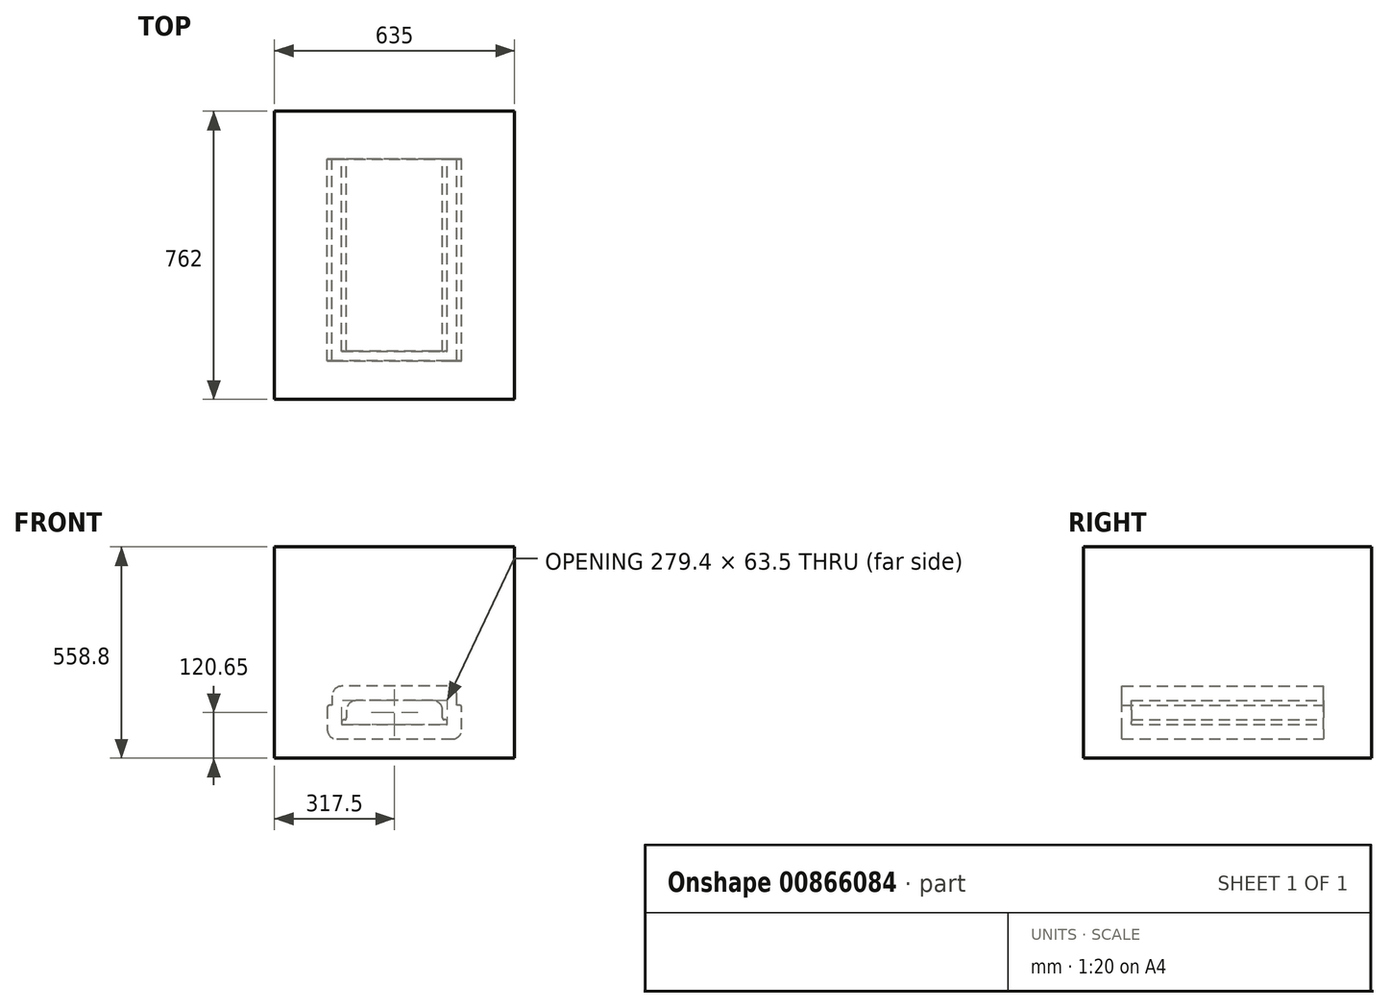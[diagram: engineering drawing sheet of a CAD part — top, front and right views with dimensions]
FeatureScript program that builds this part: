
annotation { "Feature Type Name" : "Feature", "Feature Type Description" : "" }
export const myFeature = defineFeature(function(context is Context, id is Id, definition is map)
    precondition{}
    {
        {
            var Q0;
            Q0=qCreatedBy(makeId("Front.planeOp"),FACE);
            var sketch = newSketch(context, id + "F0", { "sketchPlane" : qUnion([Q0])});
            skLineSegment(sketch, "E0", {"start": v(139.7, 0) * mm, "end": v(139.7, 12.7) * mm});
            skLineSegment(sketch, "E1", {"start": v(139.7, 12.7) * mm, "end": v(127, 12.7) * mm});
            skLineSegment(sketch, "E2", {"start": v(127, 12.7) * mm, "end": v(127, 63.5) * mm});
            skLineSegment(sketch, "E3", {"start": v(127, 63.5) * mm, "end": v(-127, 63.5) * mm});
            skLineSegment(sketch, "E4", {"start": v(-127, 63.5) * mm, "end": v(-127, 12.7) * mm});
            skLineSegment(sketch, "E5", {"start": v(-127, 12.7) * mm, "end": v(-139.7, 12.7) * mm});
            skLineSegment(sketch, "E6", {"start": v(-139.7, 12.7) * mm, "end": v(-139.7, 0) * mm});
            skLineSegment(sketch, "E7", {"start": v(0, 0) * mm, "end": v(0, 63.5) * mm, "construction": true});
            skLineSegment(sketch, "E8.0", {"start": v(-177.8, 50.8) * mm, "end": v(-177.8, 0) * mm});
            skLineSegment(sketch, "E8.1", {"start": v(-165.1, 50.8) * mm, "end": v(-177.8, 50.8) * mm});
            skLineSegment(sketch, "E8.2", {"start": v(-165.1, 101.6) * mm, "end": v(-165.1, 50.8) * mm});
            skLineSegment(sketch, "E8.3", {"start": v(177.8, 0) * mm, "end": v(177.8, 50.8) * mm});
            skLineSegment(sketch, "E8.4", {"start": v(177.8, 50.8) * mm, "end": v(165.1, 50.8) * mm});
            skLineSegment(sketch, "E8.5", {"start": v(165.1, 50.8) * mm, "end": v(165.1, 101.6) * mm});
            skLineSegment(sketch, "E8.6", {"start": v(165.1, 101.6) * mm, "end": v(-165.1, 101.6) * mm});
            skLineSegment(sketch, "E9", {"start": v(-177.8, 0) * mm, "end": v(-139.7, 0) * mm});
            skLineSegment(sketch, "E10", {"start": v(139.7, 0) * mm, "end": v(177.8, 0) * mm});
            skSolve(sketch);
        }
        {
            var Q0;
            Q0 = qSketchRegion(id + "F0", true);
            var Q1;
            Q1 = qConstructionFilter(qBodyType(qCreatedBy(id + "F0" ,EDGE), BodyType.WIRE), ConstructionObject.NO);
            extrude(context, id + "F1", {"entities" : qUnion([Q0]), "surfaceEntities" : qUnion([Q1]), "endBound" : BoundingType.SYMMETRIC, "depth" : 508 * mm, "offsetDistance" : 25.4 * mm});
        }
        {
            var Q0;
            Q0=makeQuery(id+"F1.opExtrude","SWEPT_FACE",FACE,{"disambiguationData":[OSD([sQuery(id+"F0.wireOp",EDGE,"E9")])]});
            var sketch = newSketch(context, id + "F2", { "sketchPlane" : qUnion([Q0])});
            skLineSegment(sketch, "E11.bottom", {"start": v(-177.8, 254) * mm, "end": v(177.8, 254) * mm});
            skLineSegment(sketch, "E11.top", {"start": v(-177.8, -254) * mm, "end": v(177.8, -254) * mm});
            skLineSegment(sketch, "E11.left", {"start": v(-177.8, 254) * mm, "end": v(-177.8, -254) * mm});
            skLineSegment(sketch, "E11.right", {"start": v(177.8, 254) * mm, "end": v(177.8, -254) * mm});
            skSolve(sketch);
        }
        {
            var Q0;
            Q0 = qSketchRegion(id + "F2", true);
            extrude(context, id + "F3", {"entities" : qUnion([Q0]), "operationType" : NewBodyOperationType.ADD, "depth" : 38.1 * mm, "offsetDistance" : 25.4 * mm});
        }
        {
            var Q0;
            Q0=makeQuery(id+"F1.opExtrude","SWEPT_EDGE",EDGE,{"disambiguationData":[OSD([sQuery(id+"F0.wireOp",EDGE,"E4"),sQuery(id+"F0.wireOp",EDGE,"E5")])]});
            var Q1;
            Q1=makeQuery(id+"F1.opExtrude","SWEPT_EDGE",EDGE,{"disambiguationData":[OSD([sQuery(id+"F0.wireOp",EDGE,"E1"),sQuery(id+"F0.wireOp",EDGE,"E2")])]});
            var Q2;
            Q2=makeQuery(id+"F1.opExtrude","SWEPT_EDGE",EDGE,{"disambiguationData":[OSD([sQuery(id+"F0.wireOp",EDGE,"E0"),sQuery(id+"F0.wireOp",EDGE,"E1")])]});
            var Q3;
            Q3=makeQuery(id+"F1.opExtrude","SWEPT_EDGE",EDGE,{"disambiguationData":[OSD([sQuery(id+"F0.wireOp",EDGE,"E0"),sQuery(id+"F0.wireOp",EDGE,"E10")])]});
            var Q4;
            Q4=makeQuery(id+"F1.opExtrude","SWEPT_EDGE",EDGE,{"disambiguationData":[OSD([sQuery(id+"F0.wireOp",EDGE,"E5"),sQuery(id+"F0.wireOp",EDGE,"E6")])]});
            var Q5;
            Q5=makeQuery(id+"F1.opExtrude","SWEPT_EDGE",EDGE,{"disambiguationData":[OSD([sQuery(id+"F0.wireOp",EDGE,"E6"),sQuery(id+"F0.wireOp",EDGE,"E9")])]});
            var Q6;
            Q6=makeQuery(id+"F1.opExtrude","SWEPT_EDGE",EDGE,{"disambiguationData":[OSD([sQuery(id+"F0.wireOp",EDGE,"E8.0"),sQuery(id+"F0.wireOp",EDGE,"E8.1")])]});
            var Q7;
            Q7=makeQuery(id+"F1.opExtrude","SWEPT_EDGE",EDGE,{"disambiguationData":[OSD([sQuery(id+"F0.wireOp",EDGE,"E8.3"),sQuery(id+"F0.wireOp",EDGE,"E8.4")])]});
            fillet(context, id + "F4", {"entities" : qUnion([Q0, Q1, Q2, Q3, Q4, Q5, Q6, Q7]), "radius" : 5.08 * mm, "tangentPropagation" : true, "allowEdgeOverflow" : false});
        }
        {
            var Q0;
            Q0=makeQuery(id+"F1.opExtrude","SWEPT_EDGE",EDGE,{"disambiguationData":[OSD([sQuery(id+"F0.wireOp",EDGE,"E3"),sQuery(id+"F0.wireOp",EDGE,"E4")])]});
            var Q1;
            Q1=makeQuery(id+"F1.opExtrude","SWEPT_EDGE",EDGE,{"disambiguationData":[OSD([sQuery(id+"F0.wireOp",EDGE,"E2"),sQuery(id+"F0.wireOp",EDGE,"E3")])]});
            var Q2;
            Q2=makeQuery(id+"F1.opExtrude","SWEPT_EDGE",EDGE,{"disambiguationData":[OSD([sQuery(id+"F0.wireOp",EDGE,"E8.2"),sQuery(id+"F0.wireOp",EDGE,"E8.6")])]});
            var Q3;
            Q3=makeQuery(id+"F1.opExtrude","SWEPT_EDGE",EDGE,{"disambiguationData":[OSD([sQuery(id+"F0.wireOp",EDGE,"E8.5"),sQuery(id+"F0.wireOp",EDGE,"E8.6")])]});
            var Q4;
            Q4=makeQuery(id+"F3.opExtrude","CAP_EDGE",EDGE,{"disambiguationData":[OSD([sQuery(id+"F2.wireOp",EDGE,"E11.left")])],"isStart":false});
            var Q5;
            Q5=makeQuery(id+"F3.opExtrude","CAP_EDGE",EDGE,{"disambiguationData":[OSD([sQuery(id+"F2.wireOp",EDGE,"E11.right")])],"isStart":false});
            fillet(context, id + "F5", {"entities" : qUnion([Q0, Q1, Q2, Q3, Q4, Q5]), "radius" : 25.4 * mm, "tangentPropagation" : true, "allowEdgeOverflow" : false});
        }
        {
            var Q0;
            Q0=makeQuery(id+"F3.boolean.opBoolean","MERGE",FACE,{"derivedFrom":[makeQuery(id+"F1.opExtrude","CAP_FACE",FACE,{"disambiguationData":[OSD([sQuery(id+"F0.wireOp",EDGE,"E0"),sQuery(id+"F0.wireOp",EDGE,"E1"),sQuery(id+"F0.wireOp",EDGE,"E2"),sQuery(id+"F0.wireOp",EDGE,"E3"),sQuery(id+"F0.wireOp",EDGE,"E4"),sQuery(id+"F0.wireOp",EDGE,"E5"),sQuery(id+"F0.wireOp",EDGE,"E6"),sQuery(id+"F0.wireOp",EDGE,"E8.0"),sQuery(id+"F0.wireOp",EDGE,"E8.1"),sQuery(id+"F0.wireOp",EDGE,"E8.2"),sQuery(id+"F0.wireOp",EDGE,"E8.3"),sQuery(id+"F0.wireOp",EDGE,"E8.4"),sQuery(id+"F0.wireOp",EDGE,"E8.5"),sQuery(id+"F0.wireOp",EDGE,"E8.6"),sQuery(id+"F0.wireOp",EDGE,"E9"),sQuery(id+"F0.wireOp",EDGE,"E10")])],"isStart":false}),makeQuery(id+"F3.opExtrude","SWEPT_FACE",FACE,{"disambiguationData":[OSD([sQuery(id+"F2.wireOp",EDGE,"E11.bottom")])]})]});
            var sketch = newSketch(context, id + "F6", { "sketchPlane" : qUnion([Q0])});
            skLineSegment(sketch, "E12.0.0", {"start": v(-152.4, -38.1) * mm, "end": v(152.4, -38.1) * mm});
            skArc(sketch, "E12.0.1", {"start": v(152.4, -38.1) * mm, "mid": v(170.36, -30.66) * mm, "end": v(177.8, -12.7) * mm});
            skLineSegment(sketch, "E12.0.2", {"start": v(177.8, -12.7) * mm, "end": v(177.8, 45.72) * mm});
            skArc(sketch, "E12.0.3", {"start": v(177.8, 45.72) * mm, "mid": v(176.31, 49.31) * mm, "end": v(172.72, 50.8) * mm});
            skLineSegment(sketch, "E12.0.4", {"start": v(172.72, 50.8) * mm, "end": v(165.1, 50.8) * mm});
            skLineSegment(sketch, "E12.0.5", {"start": v(165.1, 50.8) * mm, "end": v(165.1, 76.2) * mm});
            skArc(sketch, "E12.0.6", {"start": v(165.1, 76.2) * mm, "mid": v(157.66, 94.16) * mm, "end": v(139.7, 101.6) * mm});
            skLineSegment(sketch, "E12.0.7", {"start": v(139.7, 101.6) * mm, "end": v(-139.7, 101.6) * mm});
            skArc(sketch, "E12.0.8", {"start": v(-139.7, 101.6) * mm, "mid": v(-157.66, 94.16) * mm, "end": v(-165.1, 76.2) * mm});
            skLineSegment(sketch, "E12.0.9", {"start": v(-165.1, 76.2) * mm, "end": v(-165.1, 50.8) * mm});
            skLineSegment(sketch, "E12.0.10", {"start": v(-165.1, 50.8) * mm, "end": v(-172.72, 50.8) * mm});
            skArc(sketch, "E12.0.11", {"start": v(-172.72, 50.8) * mm, "mid": v(-176.31, 49.31) * mm, "end": v(-177.8, 45.72) * mm});
            skLineSegment(sketch, "E12.0.12", {"start": v(-177.8, 45.72) * mm, "end": v(-177.8, -12.7) * mm});
            skArc(sketch, "E12.0.13", {"start": v(-177.8, -12.7) * mm, "mid": v(-170.36, -30.66) * mm, "end": v(-152.4, -38.1) * mm});
            skSolve(sketch);
        }
        {
            var Q0;
            Q0 = qSketchRegion(id + "F6", true);
            extrude(context, id + "F7", {"entities" : qUnion([Q0]), "operationType" : NewBodyOperationType.ADD, "depth" : 25.4 * mm, "offsetDistance" : 25.4 * mm});
        }
        {
            var Q0;
            {var subQ0=sQuery(id+"F6.wireOp",EDGE,"E12.0.0");Q0=makeQuery(id+"FauMDgtaRmQGi94_1.1.F7.boolean.opBoolean","MERGE",FACE,{"derivedFrom":[makeQuery(id+"F7.boolean.opBoolean","MERGE",FACE,{"derivedFrom":[makeQuery(id+"F3.opExtrude","CAP_FACE",FACE,{"disambiguationData":[OSD([sQuery(id+"F2.wireOp",EDGE,"E11.bottom"),sQuery(id+"F2.wireOp",EDGE,"E11.top"),sQuery(id+"F2.wireOp",EDGE,"E11.left"),sQuery(id+"F2.wireOp",EDGE,"E11.right")])],"isStart":false}),makeQuery(id+"F7.opExtrude","SWEPT_FACE",FACE,{"disambiguationData":[OSD([subQ0])]})]}),makeQuery(id+"FauMDgtaRmQGi94_1.1.F7.opExtrude","SWEPT_FACE",FACE,{"disambiguationData":[OSD([subQ0])]})]});}
            var sketch = newSketch(context, id + "F8", { "sketchPlane" : qUnion([Q0])});
            skLineSegment(sketch, "E13.bottom", {"start": v(317.5, -381) * mm, "end": v(-317.5, -381) * mm});
            skLineSegment(sketch, "E13.top", {"start": v(317.5, 381) * mm, "end": v(-317.5, 381) * mm});
            skLineSegment(sketch, "E13.left", {"start": v(317.5, -381) * mm, "end": v(317.5, 381) * mm});
            skLineSegment(sketch, "E13.right", {"start": v(-317.5, -381) * mm, "end": v(-317.5, 381) * mm});
            skPoint(sketch, "E13.middle", {"position": v(0, 0) * mm});
            skSolve(sketch);
        }
        {
            var Q0;
            Q0 = qSketchRegion(id + "F8", true);
            extrude(context, id + "F9", {"entities" : qUnion([Q0]), "depth" : 50.8 * mm, "offsetDistance" : 25.4 * mm, "hasSecondDirection" : true, "secondDirectionOppositeDirection" : true, "secondDirectionDepth" : 508 * mm});
        }
        {
            var Q0;
            Q0=makeQuery(id+"F1.opExtrude","SWEPT_BODY",BODY,{"disambiguationData":[OSD([sQuery(id+"F0.wireOp",EDGE,"E0"),sQuery(id+"F0.wireOp",EDGE,"E1"),sQuery(id+"F0.wireOp",EDGE,"E2"),sQuery(id+"F0.wireOp",EDGE,"E3"),sQuery(id+"F0.wireOp",EDGE,"E4"),sQuery(id+"F0.wireOp",EDGE,"E5"),sQuery(id+"F0.wireOp",EDGE,"E6"),sQuery(id+"F0.wireOp",EDGE,"E8.0"),sQuery(id+"F0.wireOp",EDGE,"E8.1"),sQuery(id+"F0.wireOp",EDGE,"E8.2"),sQuery(id+"F0.wireOp",EDGE,"E8.3"),sQuery(id+"F0.wireOp",EDGE,"E8.4"),sQuery(id+"F0.wireOp",EDGE,"E8.5"),sQuery(id+"F0.wireOp",EDGE,"E8.6"),sQuery(id+"F0.wireOp",EDGE,"E9"),sQuery(id+"F0.wireOp",EDGE,"E10")])]});
            var Q1;
            Q1=makeQuery(id+"F9.opExtrude","SWEPT_BODY",BODY,{"disambiguationData":[OSD([sQuery(id+"F8.wireOp",EDGE,"E13.bottom"),sQuery(id+"F8.wireOp",EDGE,"E13.top"),sQuery(id+"F8.wireOp",EDGE,"E13.left"),sQuery(id+"F8.wireOp",EDGE,"E13.right")])]});
            booleanBodies(context, id + "F10", {"operationType" : BooleanOperationType.SUBTRACTION, "tools" : qUnion([Q0]), "targets" : qUnion([Q1]), "keepTools" : true});
        }
    });
